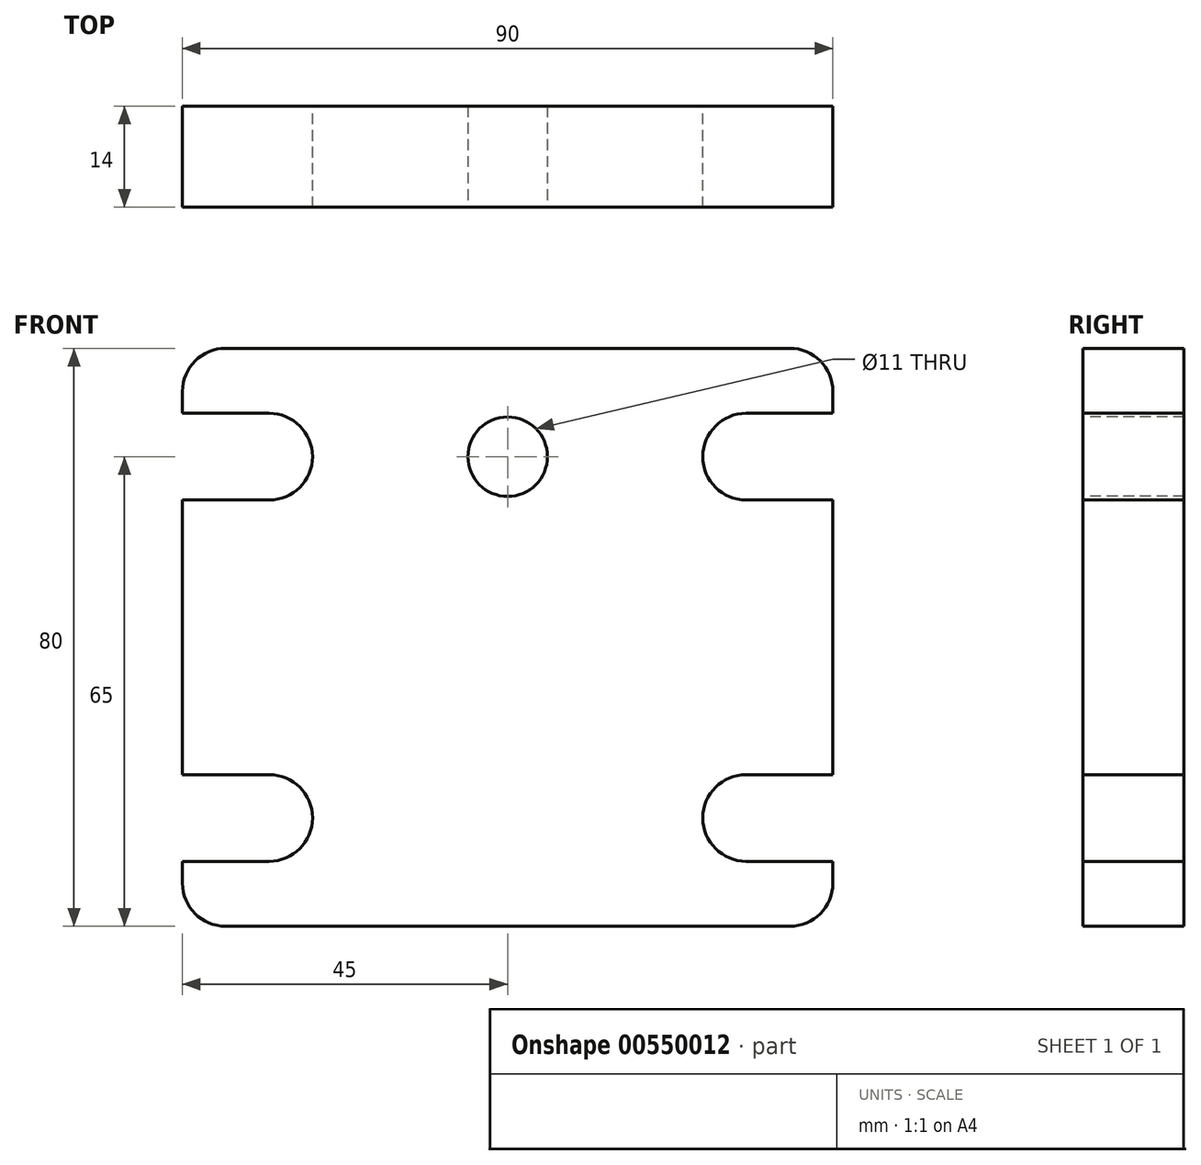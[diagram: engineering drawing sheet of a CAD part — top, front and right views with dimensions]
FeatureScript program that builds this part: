
annotation { "Feature Type Name" : "Feature", "Feature Type Description" : "" }
export const myFeature = defineFeature(function(context is Context, id is Id, definition is map)
    precondition{}
    {
        {
            var Q0;
            Q0=qCreatedBy(makeId("Front.planeOp"),FACE);
            var sketch = newSketch(context, id + "F0", { "sketchPlane" : qUnion([Q0])});
            skLineSegment(sketch, "E0.bottom", {"start": v(45, 40) * mm, "end": v(-45, 40) * mm});
            skLineSegment(sketch, "E0.top", {"start": v(45, -40) * mm, "end": v(-45, -40) * mm});
            skLineSegment(sketch, "E0.left", {"start": v(45, 40) * mm, "end": v(45, 31) * mm});
            skLineSegment(sketch, "E0.right", {"start": v(-45, 40) * mm, "end": v(-45, 31) * mm});
            skPoint(sketch, "E0.middle", {"position": v(0, 0) * mm});
            skLineSegment(sketch, "E1", {"start": v(-45, -19) * mm, "end": v(-33, -19) * mm});
            skLineSegment(sketch, "E2", {"start": v(-45, -31) * mm, "end": v(-33, -31) * mm});
            skArc(sketch, "E3", {"start": v(-33, -31) * mm, "mid": v(-27, -25) * mm, "end": v(-33, -19) * mm});
            skLineSegment(sketch, "E4.trimOffspring", {"start": v(-45, -31) * mm, "end": v(-45, -40) * mm});
            skLineSegment(sketch, "E5.MirrorCS", {"start": v(45, -19) * mm, "end": v(33, -19) * mm});
            skArc(sketch, "E6.MirrorCS", {"start": v(33, -31) * mm, "mid": v(27, -25) * mm, "end": v(33, -19) * mm});
            skLineSegment(sketch, "E7.MirrorCS", {"start": v(45, -31) * mm, "end": v(33, -31) * mm});
            skLineSegment(sketch, "E8.MirrorCS", {"start": v(-45, 19) * mm, "end": v(-33, 19) * mm});
            skArc(sketch, "E9.MirrorCS", {"start": v(-33, 31) * mm, "mid": v(-27, 25) * mm, "end": v(-33, 19) * mm});
            skLineSegment(sketch, "E10.MirrorCS", {"start": v(-45, 31) * mm, "end": v(-33, 31) * mm});
            skLineSegment(sketch, "E11.MirrorCS", {"start": v(45, 19) * mm, "end": v(33, 19) * mm});
            skArc(sketch, "E12.MirrorCS", {"start": v(33, 31) * mm, "mid": v(27, 25) * mm, "end": v(33, 19) * mm});
            skLineSegment(sketch, "E13.MirrorCS", {"start": v(45, 31) * mm, "end": v(33, 31) * mm});
            skLineSegment(sketch, "E14.trimOffspring", {"start": v(-45, 19) * mm, "end": v(-45, -19) * mm});
            skLineSegment(sketch, "E15.trimOffspring", {"start": v(45, 19) * mm, "end": v(45, -19) * mm});
            skLineSegment(sketch, "E16.trimOffspring", {"start": v(45, -31) * mm, "end": v(45, -40) * mm});
            skSolve(sketch);
        }
        {
            var Q0;
            Q0 = qSketchRegion(id + "F0", true);
            extrude(context, id + "F1", {"entities" : qUnion([Q0]), "depth" : 14 * mm, "offsetDistance" : 25 * mm});
        }
        {
            var Q0;
            Q0=makeQuery(id+"F1.opExtrude","SWEPT_EDGE",EDGE,{"disambiguationData":[OSD([sQuery(id+"F0.wireOp",EDGE,"E0.bottom"),sQuery(id+"F0.wireOp",EDGE,"E0.right")])]});
            var Q1;
            Q1=makeQuery(id+"F1.opExtrude","SWEPT_EDGE",EDGE,{"disambiguationData":[OSD([sQuery(id+"F0.wireOp",EDGE,"E0.top"),sQuery(id+"F0.wireOp",EDGE,"E4.trimOffspring")])]});
            var Q2;
            Q2=makeQuery(id+"F1.opExtrude","SWEPT_EDGE",EDGE,{"disambiguationData":[OSD([sQuery(id+"F0.wireOp",EDGE,"E0.bottom"),sQuery(id+"F0.wireOp",EDGE,"E0.left")])]});
            var Q3;
            Q3=makeQuery(id+"F1.opExtrude","SWEPT_EDGE",EDGE,{"disambiguationData":[OSD([sQuery(id+"F0.wireOp",EDGE,"E0.top"),sQuery(id+"F0.wireOp",EDGE,"E16.trimOffspring")])]});
            fillet(context, id + "F2", {"entities" : qUnion([Q0, Q1, Q2, Q3]), "radius" : 6 * mm, "tangentPropagation" : true, "allowEdgeOverflow" : false});
        }
        {
            var Q0;
            Q0=makeQuery(id+"F1.opExtrude","CAP_FACE",FACE,{"disambiguationData":[OSD([sQuery(id+"F0.wireOp",EDGE,"E0.bottom"),sQuery(id+"F0.wireOp",EDGE,"E0.top"),sQuery(id+"F0.wireOp",EDGE,"E0.left"),sQuery(id+"F0.wireOp",EDGE,"E0.right"),sQuery(id+"F0.wireOp",EDGE,"E1"),sQuery(id+"F0.wireOp",EDGE,"E2"),sQuery(id+"F0.wireOp",EDGE,"E3"),sQuery(id+"F0.wireOp",EDGE,"E4.trimOffspring"),sQuery(id+"F0.wireOp",EDGE,"E5.MirrorCS"),sQuery(id+"F0.wireOp",EDGE,"E6.MirrorCS"),sQuery(id+"F0.wireOp",EDGE,"E7.MirrorCS"),sQuery(id+"F0.wireOp",EDGE,"E8.MirrorCS"),sQuery(id+"F0.wireOp",EDGE,"E9.MirrorCS"),sQuery(id+"F0.wireOp",EDGE,"E10.MirrorCS"),sQuery(id+"F0.wireOp",EDGE,"E11.MirrorCS"),sQuery(id+"F0.wireOp",EDGE,"E12.MirrorCS"),sQuery(id+"F0.wireOp",EDGE,"E13.MirrorCS"),sQuery(id+"F0.wireOp",EDGE,"E14.trimOffspring"),sQuery(id+"F0.wireOp",EDGE,"E15.trimOffspring"),sQuery(id+"F0.wireOp",EDGE,"E16.trimOffspring")])],"isStart":false});
            var sketch = newSketch(context, id + "F3", { "sketchPlane" : qUnion([Q0])});
            skPoint(sketch, "E17", {"position": v(0, 25) * mm});
            skSolve(sketch);
        }
        {
            var Q0;
            Q0=sQuery(id+"F3.wireOp",VERTEX,"E17");
            var Q1;
            Q1=makeQuery(id+"F1.opExtrude","SWEPT_BODY",BODY,{"disambiguationData":[OSD([sQuery(id+"F0.wireOp",EDGE,"E0.bottom"),sQuery(id+"F0.wireOp",EDGE,"E0.top"),sQuery(id+"F0.wireOp",EDGE,"E0.left"),sQuery(id+"F0.wireOp",EDGE,"E0.right"),sQuery(id+"F0.wireOp",EDGE,"E1"),sQuery(id+"F0.wireOp",EDGE,"E2"),sQuery(id+"F0.wireOp",EDGE,"E3"),sQuery(id+"F0.wireOp",EDGE,"E4.trimOffspring"),sQuery(id+"F0.wireOp",EDGE,"E5.MirrorCS"),sQuery(id+"F0.wireOp",EDGE,"E6.MirrorCS"),sQuery(id+"F0.wireOp",EDGE,"E7.MirrorCS"),sQuery(id+"F0.wireOp",EDGE,"E8.MirrorCS"),sQuery(id+"F0.wireOp",EDGE,"E9.MirrorCS"),sQuery(id+"F0.wireOp",EDGE,"E10.MirrorCS"),sQuery(id+"F0.wireOp",EDGE,"E11.MirrorCS"),sQuery(id+"F0.wireOp",EDGE,"E12.MirrorCS"),sQuery(id+"F0.wireOp",EDGE,"E13.MirrorCS"),sQuery(id+"F0.wireOp",EDGE,"E14.trimOffspring"),sQuery(id+"F0.wireOp",EDGE,"E15.trimOffspring"),sQuery(id+"F0.wireOp",EDGE,"E16.trimOffspring")])]});
            hole(context, id + "F4", {"style" : HoleStyle.SIMPLE, "endStyle" : HoleEndStyle.THROUGH, "holeDiameter" : 11 * mm, "isTappedThrough" : true, "tappedDepth" : 12 * mm, "tapClearance" : 3, "locations" : qUnion([Q0]), "scope" : qUnion([Q1])});
        }
    });
